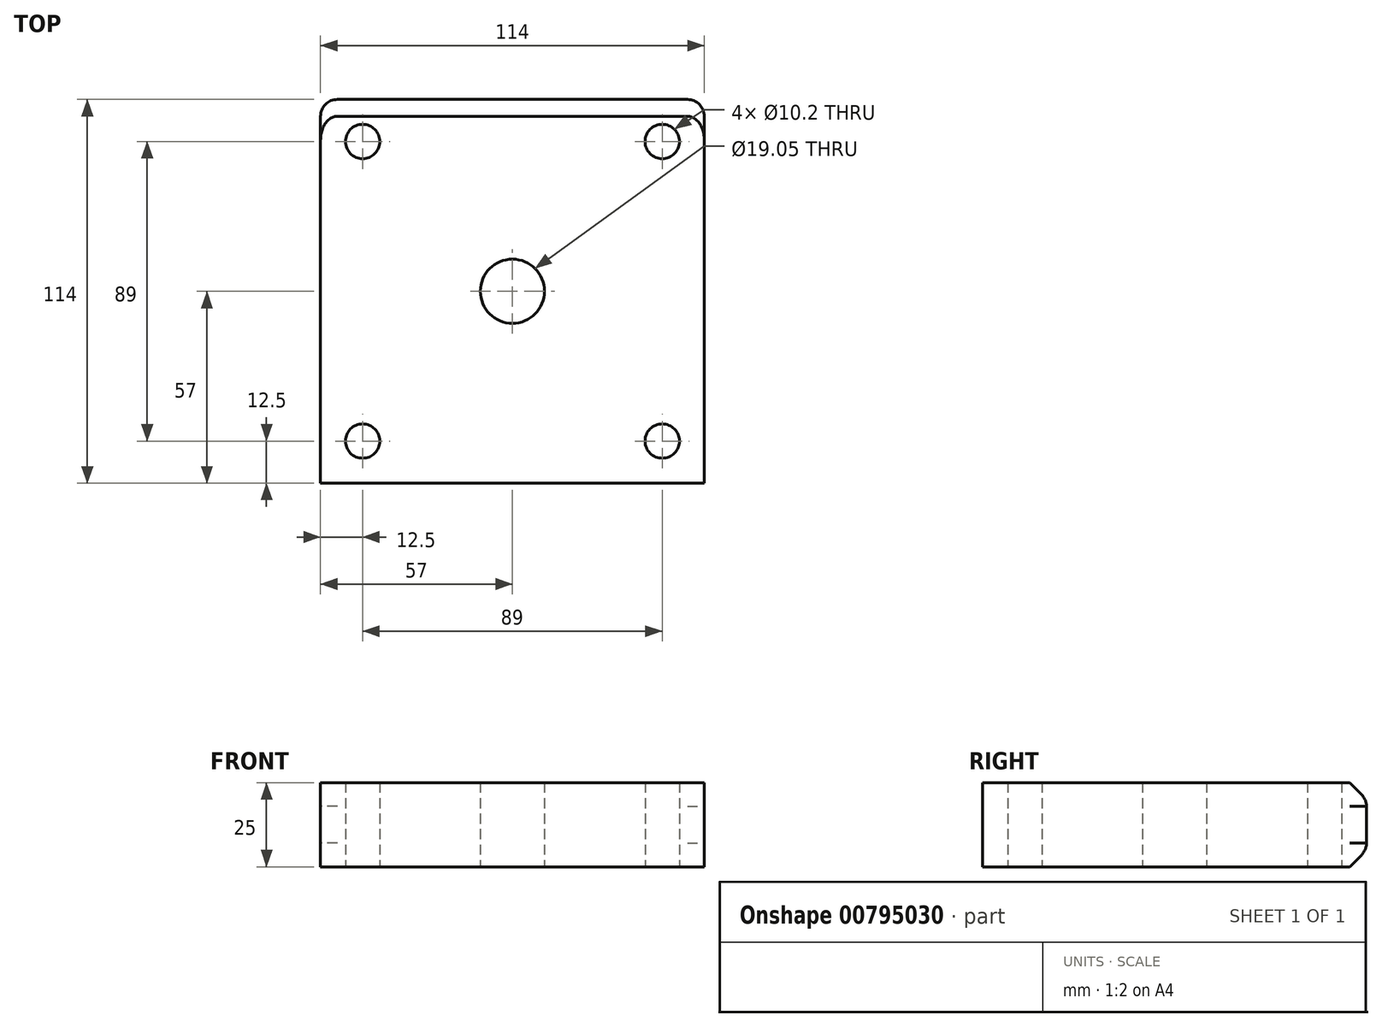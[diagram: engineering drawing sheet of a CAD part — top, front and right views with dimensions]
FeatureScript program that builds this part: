
annotation { "Feature Type Name" : "Feature", "Feature Type Description" : "" }
export const myFeature = defineFeature(function(context is Context, id is Id, definition is map)
    precondition{}
    {
        {
            var Q0;
            Q0=qCreatedBy(makeId("Top.planeOp"),FACE);
            var sketch = newSketch(context, id + "F0", { "sketchPlane" : qUnion([Q0])});
            skLineSegment(sketch, "E0.bottom", {"start": v(57, -57) * mm, "end": v(-57, -57) * mm});
            skLineSegment(sketch, "E0.top", {"start": v(57, 57) * mm, "end": v(-57, 57) * mm});
            skLineSegment(sketch, "E0.left", {"start": v(57, -57) * mm, "end": v(57, 57) * mm});
            skLineSegment(sketch, "E0.right", {"start": v(-57, -57) * mm, "end": v(-57, 57) * mm});
            skPoint(sketch, "E0.middle", {"position": v(0, 0) * mm});
            skCircle(sketch, "E1", {"center": v(0, 0) * mm, "radius": 9.53 * mm});
            skCircle(sketch, "E2", {"center": v(-44.5, 44.5) * mm, "radius": 5.1 * mm});
            skCircle(sketch, "E3.0.1.0", {"center": v(-44.5, -44.5) * mm, "radius": 5.1 * mm});
            skCircle(sketch, "E3.1.0.0", {"center": v(44.5, 44.5) * mm, "radius": 5.1 * mm});
            skCircle(sketch, "E3.1.1.0", {"center": v(44.5, -44.5) * mm, "radius": 5.1 * mm});
            skLineSegment(sketch, "E3.direction1", {"start": v(-44.5, 44.5) * mm, "end": v(44.5, 44.5) * mm, "construction": true});
            skLineSegment(sketch, "E3.direction2", {"start": v(-44.5, 44.5) * mm, "end": v(-44.5, -44.5) * mm, "construction": true});
            skSolve(sketch);
        }
        {
            var Q0;
            Q0=makeQuery(id+"F0.imprint","IMPRINT",FACE,{"disambiguationData":[TD([[makeQuery(id+"F0.imprint","IMPRINT",EDGE,{"derivedFrom":sQuery(id+"F0.wireOp",EDGE,"E0.bottom")}),-1.0]])]});
            extrude(context, id + "F1", {"entities" : qUnion([Q0]), "depth" : 25 * mm, "offsetDistance" : 25 * mm});
        }
        {
            var Q0;
            Q0=makeQuery(id+"F1.opExtrude","CAP_EDGE",EDGE,{"disambiguationData":[OSD([sQuery(id+"F0.wireOp",EDGE,"E0.top")])],"isStart":true});
            var Q1;
            Q1=makeQuery(id+"F1.opExtrude","CAP_EDGE",EDGE,{"disambiguationData":[OSD([sQuery(id+"F0.wireOp",EDGE,"E0.top")])],"isStart":false});
            chamfer(context, id + "F2", {"entities" : qUnion([Q0, Q1]), "width" : 5 * mm, "tangentPropagation" : true});
        }
        {
            var Q0;
            Q0=makeQuery(id+"F1.opExtrude","SWEPT_EDGE",EDGE,{"disambiguationData":[OSD([sQuery(id+"F0.wireOp",EDGE,"E0.top"),sQuery(id+"F0.wireOp",EDGE,"E0.right")])]});
            var Q1;
            Q1=makeQuery(id+"F1.opExtrude","SWEPT_EDGE",EDGE,{"disambiguationData":[OSD([sQuery(id+"F0.wireOp",EDGE,"E0.top"),sQuery(id+"F0.wireOp",EDGE,"E0.left")])]});
            fillet(context, id + "F3", {"entities" : qUnion([Q0, Q1]), "radius" : 5 * mm, "tangentPropagation" : true, "allowEdgeOverflow" : false});
        }
        {
            var Q0;
            {var subQ0=sQuery(id+"F0.wireOp",EDGE,"E0.top");Q0=makeQuery(id+"F3.opFillet","BLEND_EDGE",EDGE,{"blendedFrom":[makeQuery(id+"F1.opExtrude","SWEPT_EDGE",EDGE,{"disambiguationData":[OSD([subQ0,sQuery(id+"F0.wireOp",EDGE,"E0.right")])]}),makeQuery(id+"F2.opChamfer","BLEND_FACE",FACE,{"disambiguationData":[OSD([subQ0]),TDD([makeQuery(id+"F1.opExtrude","CAP_EDGE",EDGE,{"disambiguationData":[OSD([subQ0])],"isStart":true})])]})],"blendedInto":[makeQuery(id+"F2.opChamfer","BLEND_FACE",FACE,{"disambiguationData":[OSD([subQ0]),TDD([makeQuery(id+"F1.opExtrude","CAP_EDGE",EDGE,{"disambiguationData":[OSD([subQ0])],"isStart":true})])]})]});}
            var Q1;
            {var subQ0=sQuery(id+"F0.wireOp",EDGE,"E0.top");Q1=makeQuery(id+"F3.opFillet","BLEND_EDGE",EDGE,{"blendedFrom":[makeQuery(id+"F1.opExtrude","SWEPT_EDGE",EDGE,{"disambiguationData":[OSD([subQ0,sQuery(id+"F0.wireOp",EDGE,"E0.right")])]}),makeQuery(id+"F2.opChamfer","BLEND_FACE",FACE,{"disambiguationData":[OSD([subQ0]),TDD([makeQuery(id+"F1.opExtrude","CAP_EDGE",EDGE,{"disambiguationData":[OSD([subQ0])],"isStart":false})])]})],"blendedInto":[makeQuery(id+"F2.opChamfer","BLEND_FACE",FACE,{"disambiguationData":[OSD([subQ0]),TDD([makeQuery(id+"F1.opExtrude","CAP_EDGE",EDGE,{"disambiguationData":[OSD([subQ0])],"isStart":false})])]})]});}
            fillet(context, id + "F4", {"entities" : qUnion([Q0, Q1]), "radius" : 5 * mm, "tangentPropagation" : true, "allowEdgeOverflow" : false});
        }
    });
